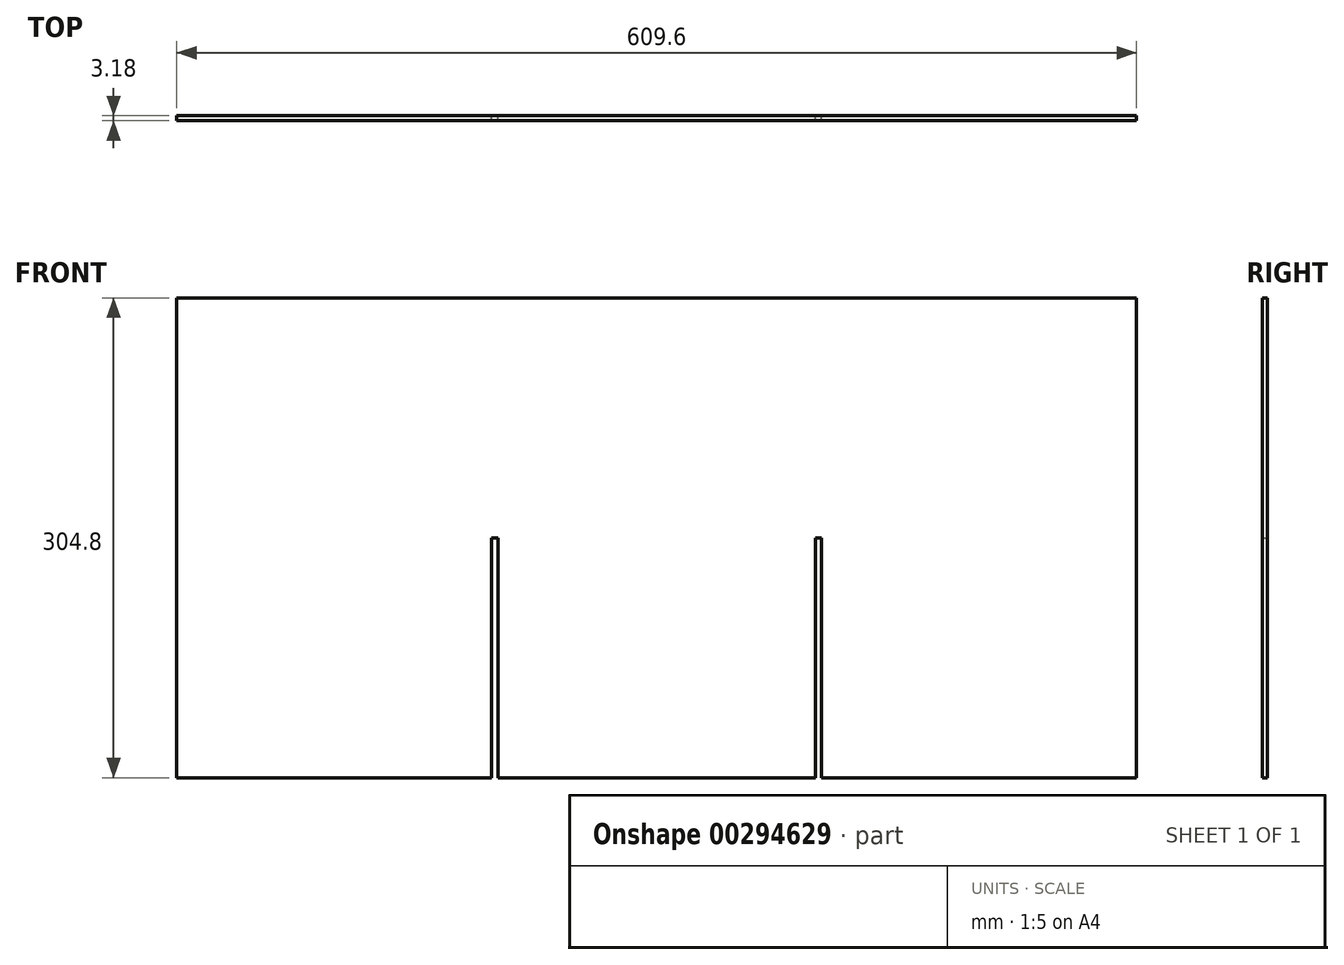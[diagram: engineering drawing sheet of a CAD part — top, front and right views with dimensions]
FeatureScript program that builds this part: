
annotation { "Feature Type Name" : "Feature", "Feature Type Description" : "" }
export const myFeature = defineFeature(function(context is Context, id is Id, definition is map)
    precondition{}
    {
        {
            var Q0;
            Q0=qCreatedBy(makeId("Front.planeOp"),FACE);
            var sketch = newSketch(context, id + "F0", { "sketchPlane" : qUnion([Q0])});
            skLineSegment(sketch, "E0.bottom", {"start": v(-310.6, 45.05) * mm, "end": v(299, 45.05) * mm});
            skLineSegment(sketch, "E0.top", {"start": v(-310.6, -259.75) * mm, "end": v(299, -259.75) * mm});
            skLineSegment(sketch, "E0.left", {"start": v(-310.6, 45.05) * mm, "end": v(-310.6, -259.75) * mm});
            skLineSegment(sketch, "E0.right", {"start": v(299, 45.05) * mm, "end": v(299, -259.75) * mm});
            skSolve(sketch);
        }
        {
            var Q0;
            Q0 = qSketchRegion(id + "F0", true);
            extrude(context, id + "F1", {"entities" : qUnion([Q0]), "endBound" : BoundingType.SYMMETRIC, "depth" : 3.17 * mm});
        }
        {
            var Q0;
            Q0=makeQuery(id+"F1.opExtrude","SWEPT_FACE",FACE,{"disambiguationData":[OSD([sQuery(id+"F0.wireOp",EDGE,"E0.top")])]});
            var sketch = newSketch(context, id + "F2", { "sketchPlane" : qUnion([Q0])});
            skLineSegment(sketch, "E1.bottom", {"start": v(95, 1.59) * mm, "end": v(98.97, 1.59) * mm});
            skLineSegment(sketch, "E1.top", {"start": v(95, -1.59) * mm, "end": v(98.97, -1.59) * mm});
            skLineSegment(sketch, "E1.left", {"start": v(95, 1.59) * mm, "end": v(95, -1.59) * mm});
            skLineSegment(sketch, "E1.right", {"start": v(98.97, 1.59) * mm, "end": v(98.97, -1.59) * mm});
            skSolve(sketch);
        }
        {
            var Q0;
            Q0 = qSketchRegion(id + "F2", true);
            extrude(context, id + "F3", {"entities" : qUnion([Q0]), "operationType" : NewBodyOperationType.REMOVE, "oppositeDirection" : true, "depth" : 152.4 * mm});
        }
        {
            var Q0;
            {var subQ1=sQuery(id+"F0.wireOp",EDGE,"E0.left");var subQ2=sQuery(id+"F0.wireOp",EDGE,"E0.top");Q0=makeQuery(id+"F3.boolean.opBoolean","SPLIT",FACE,{"disambiguationData":[TD([makeQuery(id+"F1.opExtrude","SWEPT_FACE",FACE,{"disambiguationData":[OSD([subQ1])]})])],"derivedFrom":makeQuery(id+"F1.opExtrude","SWEPT_FACE",FACE,{"disambiguationData":[OSD([subQ2])]})});}
            var sketch = newSketch(context, id + "F4", { "sketchPlane" : qUnion([Q0])});
            skLineSegment(sketch, "E2.bottom", {"start": v(-110.58, 1.59) * mm, "end": v(-106.6, 1.59) * mm});
            skLineSegment(sketch, "E2.top", {"start": v(-110.58, -1.59) * mm, "end": v(-106.6, -1.59) * mm});
            skLineSegment(sketch, "E2.left", {"start": v(-110.58, 1.59) * mm, "end": v(-110.58, -1.59) * mm});
            skLineSegment(sketch, "E2.right", {"start": v(-106.6, 1.59) * mm, "end": v(-106.6, -1.59) * mm});
            skSolve(sketch);
        }
        {
            var Q0;
            Q0 = qSketchRegion(id + "F4", true);
            extrude(context, id + "F5", {"entities" : qUnion([Q0]), "operationType" : NewBodyOperationType.REMOVE, "oppositeDirection" : true, "depth" : 152.4 * mm});
        }
    });
